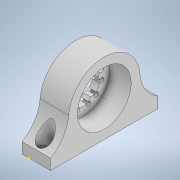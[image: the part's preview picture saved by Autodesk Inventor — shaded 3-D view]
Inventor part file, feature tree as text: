
AUTODESK INVENTOR PART (.ipt)
format: ipt  version: 2020 (Build 240168000, 168)  size: 242,688 bytes
history: native  units: in
note: dims shown in document units (in); Inventor stores cm internally (conversion verified against a paired STEP export)
features: sketch x8, extrude x6, pattern_circular x2, fillet x2, other x1, hole x1
ambient origin geometry x8: Origin, YZ Plane, XZ Plane, XY Plane, X Axis, Y Axis, Z Axis, Center Point
bodies: Solid1 (feature_tree)
feature tree (20):
  extrude  "Extrusion1"  Depth=3.0in
  extrude  "Extrusion2"  Depth=0.5in
  extrude  "Extrusion3"  Depth=0.8in
  extrude  "Extrusion4"  Depth=1.0in
  sketch  "Sketch5"  dims[d10=1.5in]
  other  "Work Axis1"
  pattern_circular  "Circular Pattern1"  Count=6 Angle=360.0deg
  fillet  "Fillet1"  Radius=1.0in
  sketch  "Sketch6"  dims[d11=0.6in d12=0.0in]
  fillet  "Fillet2"  Radius=0.25in
  hole  "Hole1"  [1 undecoded]
  extrude  "Extrusion5"  Depth=1.0in
  extrude  "Extrusion6"  Depth=0.6in
  pattern_circular  "Circular Pattern2"  [2 undecoded]
  sketch  "Sketch1"  dims[d0=0.8in d1=3.0in]
  sketch  "Sketch2"  dims[d2=0.3in d3=0.0in d4=0.5in]
  sketch  "Sketch3"  dims[d5=0.8in d6=2.0in]
  sketch  "Sketch4"  dims[d7=1.7in d8=0.0in d9=1.0in]
  sketch  "Sketch7"  dims[d13=0.25in]
  sketch  "Sketch8"  dims[d14=0.6in d15=0.0in d16=2.3622in d17=360.0deg d19=1.0in d20=0.25in d21=0.25in d22=1.0in d23=0.2in d24=0.75in d25=0.4in d26=0.15in d27=0.5635in d28=1.0in d29=0.8108in d30=0.4in d31=0.4in d32=0.6in d33=0.0in d38=0.6in d39=0.0in d40=2.3622in d41=360.0deg d43=0.055in d44=0.055in d45=0.13in d46=0.13in]
note: 3 required parameter values undecoded (feature->parameter linkage not recoverable at this tier; creation-order binding heuristic only, values carry confidence <= 0.55)
